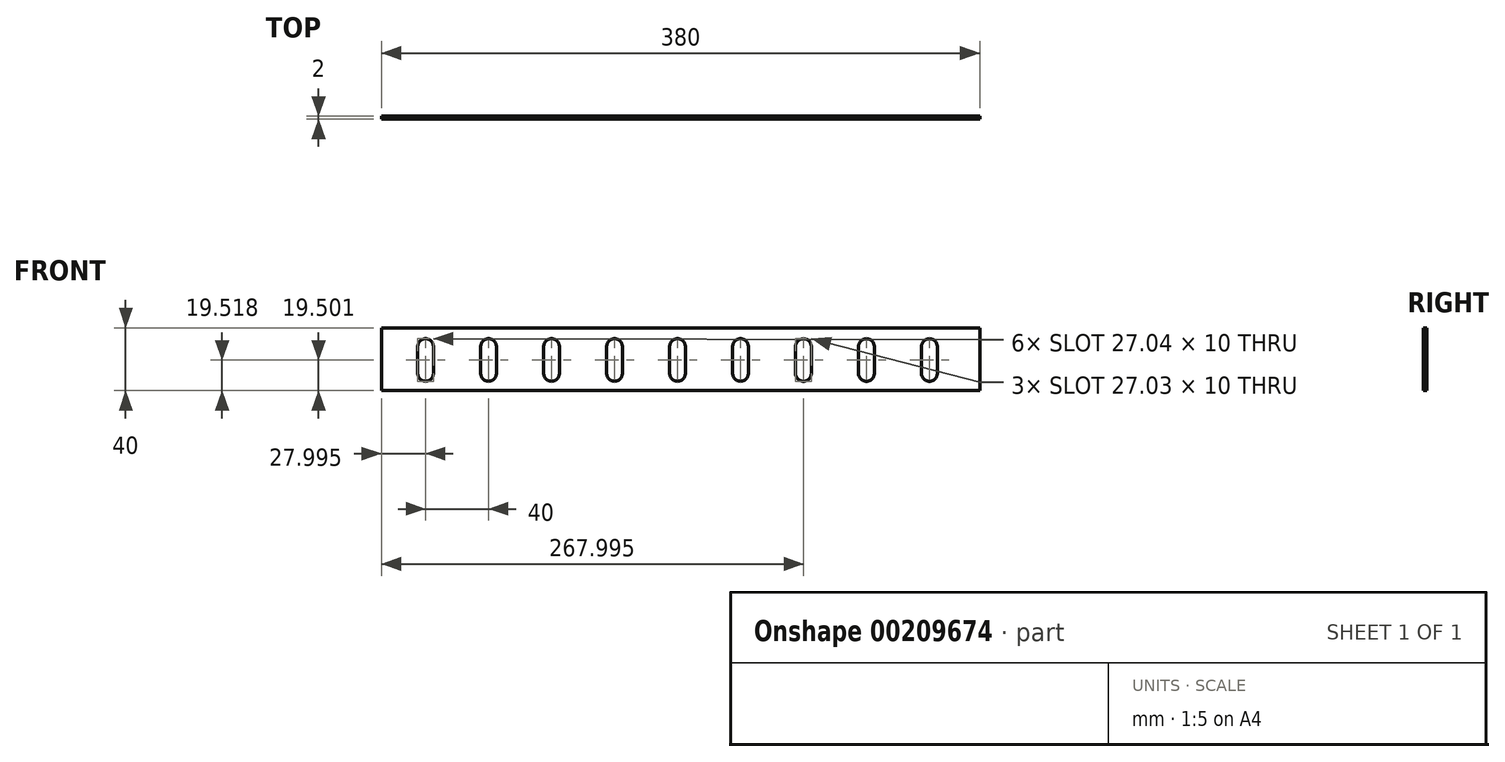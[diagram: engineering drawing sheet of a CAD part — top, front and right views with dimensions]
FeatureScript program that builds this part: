
annotation { "Feature Type Name" : "Feature", "Feature Type Description" : "" }
export const myFeature = defineFeature(function(context is Context, id is Id, definition is map)
    precondition{}
    {
        {
            var Q0;
            Q0=qCreatedBy(makeId("Front.planeOp"),FACE);
            var sketch = newSketch(context, id + "F0", { "sketchPlane" : qUnion([Q0])});
            skLineSegment(sketch, "E0.bottom", {"start": v(171.65, -9.27) * mm, "end": v(-208.35, -9.27) * mm});
            skLineSegment(sketch, "E0.top", {"start": v(171.65, 30.73) * mm, "end": v(-208.35, 30.73) * mm});
            skLineSegment(sketch, "E0.left", {"start": v(171.65, -9.27) * mm, "end": v(171.65, 30.73) * mm});
            skLineSegment(sketch, "E0.right", {"start": v(-208.35, -9.27) * mm, "end": v(-208.35, 30.73) * mm});
            skPoint(sketch, "E0.middle", {"position": v(-20.35, 11.27) * mm});
            skPoint(sketch, "E1", {"position": v(-179.24, -10.73) * mm});
            skLineSegment(sketch, "E2.bottom", {"start": v(-179.24, 21.77) * mm, "end": v(-179.24, 21.77) * mm});
            skLineSegment(sketch, "E2.left", {"start": v(-175.35, 18.77) * mm, "end": v(-175.35, 1.73) * mm});
            skLineSegment(sketch, "E2.right", {"start": v(-185.35, 18.77) * mm, "end": v(-185.35, 1.73) * mm});
            skPoint(sketch, "E3.visualSharp", {"position": v(-185.35, 23.77) * mm});
            skArc(sketch, "E3.filletArc", {"start": v(-180.35, 23.77) * mm, "mid": v(-183.9, 22.3) * mm, "end": v(-185.35, 18.77) * mm});
            skPoint(sketch, "E4.visualSharp", {"position": v(-175.35, 23.77) * mm});
            skArc(sketch, "E4.filletArc", {"start": v(-175.35, 18.77) * mm, "mid": v(-176.82, 22.3) * mm, "end": v(-180.35, 23.77) * mm});
            skPoint(sketch, "E5", {"position": v(-139.24, -10.73) * mm});
            skLineSegment(sketch, "E6.bottom", {"start": v(-139.24, 21.77) * mm, "end": v(-139.24, 21.77) * mm});
            skLineSegment(sketch, "E6.left", {"start": v(-135.35, 18.77) * mm, "end": v(-135.35, 1.73) * mm});
            skLineSegment(sketch, "E6.right", {"start": v(-145.35, 18.77) * mm, "end": v(-145.35, 1.73) * mm});
            skPoint(sketch, "E7.visualSharp", {"position": v(-145.35, 23.77) * mm});
            skArc(sketch, "E7.filletArc", {"start": v(-140.35, 23.77) * mm, "mid": v(-143.9, 22.3) * mm, "end": v(-145.35, 18.77) * mm});
            skPoint(sketch, "E8.visualSharp", {"position": v(-135.35, 23.77) * mm});
            skArc(sketch, "E8.filletArc", {"start": v(-135.35, 18.77) * mm, "mid": v(-136.82, 22.3) * mm, "end": v(-140.35, 23.77) * mm});
            skPoint(sketch, "E9", {"position": v(-99.24, -10.73) * mm});
            skLineSegment(sketch, "E10.bottom", {"start": v(-99.24, 21.77) * mm, "end": v(-99.24, 21.77) * mm});
            skLineSegment(sketch, "E10.left", {"start": v(-95.35, 18.77) * mm, "end": v(-95.35, 1.73) * mm});
            skLineSegment(sketch, "E10.right", {"start": v(-105.35, 18.77) * mm, "end": v(-105.35, 1.73) * mm});
            skPoint(sketch, "E11.visualSharp", {"position": v(-105.35, 23.77) * mm});
            skArc(sketch, "E11.filletArc", {"start": v(-100.35, 23.77) * mm, "mid": v(-103.9, 22.3) * mm, "end": v(-105.35, 18.77) * mm});
            skPoint(sketch, "E12.visualSharp", {"position": v(-95.35, 23.77) * mm});
            skArc(sketch, "E12.filletArc", {"start": v(-95.35, 18.77) * mm, "mid": v(-96.82, 22.3) * mm, "end": v(-100.35, 23.77) * mm});
            skPoint(sketch, "E13", {"position": v(-59.24, -10.73) * mm});
            skLineSegment(sketch, "E14.bottom", {"start": v(-59.24, 21.77) * mm, "end": v(-59.24, 21.77) * mm});
            skLineSegment(sketch, "E14.left", {"start": v(-55.35, 18.77) * mm, "end": v(-55.35, 1.73) * mm});
            skLineSegment(sketch, "E14.right", {"start": v(-65.35, 18.77) * mm, "end": v(-65.35, 1.73) * mm});
            skPoint(sketch, "E15.visualSharp", {"position": v(-65.35, 23.77) * mm});
            skArc(sketch, "E15.filletArc", {"start": v(-60.35, 23.77) * mm, "mid": v(-63.9, 22.3) * mm, "end": v(-65.35, 18.77) * mm});
            skPoint(sketch, "E16.visualSharp", {"position": v(-55.35, 23.77) * mm});
            skArc(sketch, "E16.filletArc", {"start": v(-55.35, 18.77) * mm, "mid": v(-56.82, 22.3) * mm, "end": v(-60.35, 23.77) * mm});
            skPoint(sketch, "E17", {"position": v(-19.24, -10.73) * mm});
            skLineSegment(sketch, "E18.bottom", {"start": v(-19.24, 21.77) * mm, "end": v(-19.24, 21.77) * mm});
            skLineSegment(sketch, "E18.left", {"start": v(-15.35, 18.77) * mm, "end": v(-15.35, 1.73) * mm});
            skLineSegment(sketch, "E18.right", {"start": v(-25.35, 18.77) * mm, "end": v(-25.35, 1.73) * mm});
            skPoint(sketch, "E19.visualSharp", {"position": v(-25.35, 23.77) * mm});
            skArc(sketch, "E19.filletArc", {"start": v(-20.35, 23.77) * mm, "mid": v(-23.9, 22.3) * mm, "end": v(-25.35, 18.77) * mm});
            skPoint(sketch, "E20.visualSharp", {"position": v(-15.35, 23.77) * mm});
            skArc(sketch, "E20.filletArc", {"start": v(-15.35, 18.77) * mm, "mid": v(-16.82, 22.3) * mm, "end": v(-20.35, 23.77) * mm});
            skPoint(sketch, "E21", {"position": v(20.76, -10.73) * mm});
            skLineSegment(sketch, "E22.bottom", {"start": v(20.76, 21.77) * mm, "end": v(20.76, 21.77) * mm});
            skLineSegment(sketch, "E22.left", {"start": v(24.65, 18.77) * mm, "end": v(24.65, 1.73) * mm});
            skLineSegment(sketch, "E22.right", {"start": v(14.65, 18.77) * mm, "end": v(14.65, 1.73) * mm});
            skPoint(sketch, "E23.visualSharp", {"position": v(14.65, 23.77) * mm});
            skArc(sketch, "E23.filletArc", {"start": v(19.65, 23.77) * mm, "mid": v(16.1, 22.3) * mm, "end": v(14.65, 18.77) * mm});
            skPoint(sketch, "E24.visualSharp", {"position": v(24.65, 23.77) * mm});
            skArc(sketch, "E24.filletArc", {"start": v(24.65, 18.77) * mm, "mid": v(23.18, 22.3) * mm, "end": v(19.65, 23.77) * mm});
            skLineSegment(sketch, "E25", {"start": v(-179.24, -5.27) * mm, "end": v(-179.24, -5.27) * mm});
            skPoint(sketch, "E26.visualSharp", {"position": v(-185.35, -3.27) * mm});
            skArc(sketch, "E26.filletArc", {"start": v(-185.35, 1.73) * mm, "mid": v(-183.9, -1.8) * mm, "end": v(-180.35, -3.27) * mm});
            skArc(sketch, "E27.filletArc", {"start": v(-180.35, -3.27) * mm, "mid": v(-176.82, -1.8) * mm, "end": v(-175.35, 1.73) * mm});
            skLineSegment(sketch, "E28", {"start": v(-139.24, -5.27) * mm, "end": v(-139.24, -5.27) * mm});
            skLineSegment(sketch, "E29", {"start": v(-99.24, -5.27) * mm, "end": v(-99.24, -5.27) * mm});
            skLineSegment(sketch, "E30", {"start": v(-59.24, -5.27) * mm, "end": v(-59.24, -5.27) * mm});
            skLineSegment(sketch, "E31", {"start": v(-19.24, -5.27) * mm, "end": v(-19.24, -5.27) * mm});
            skLineSegment(sketch, "E32", {"start": v(20.76, -5.27) * mm, "end": v(20.76, -5.27) * mm});
            skPoint(sketch, "E33.visualSharp", {"position": v(-145.35, -3.27) * mm});
            skArc(sketch, "E33.filletArc", {"start": v(-145.35, 1.73) * mm, "mid": v(-143.9, -1.8) * mm, "end": v(-140.35, -3.27) * mm});
            skPoint(sketch, "E34.visualSharp", {"position": v(-135.35, -3.27) * mm});
            skArc(sketch, "E34.filletArc", {"start": v(-140.35, -3.27) * mm, "mid": v(-136.82, -1.8) * mm, "end": v(-135.35, 1.73) * mm});
            skPoint(sketch, "E35.visualSharp", {"position": v(-105.35, -3.27) * mm});
            skArc(sketch, "E35.filletArc", {"start": v(-105.35, 1.73) * mm, "mid": v(-103.9, -1.8) * mm, "end": v(-100.35, -3.27) * mm});
            skPoint(sketch, "E36.visualSharp", {"position": v(-95.35, -3.27) * mm});
            skArc(sketch, "E36.filletArc", {"start": v(-100.35, -3.27) * mm, "mid": v(-96.82, -1.8) * mm, "end": v(-95.35, 1.73) * mm});
            skPoint(sketch, "E37.visualSharp", {"position": v(-65.35, -3.27) * mm});
            skArc(sketch, "E37.filletArc", {"start": v(-65.35, 1.73) * mm, "mid": v(-63.9, -1.8) * mm, "end": v(-60.35, -3.27) * mm});
            skPoint(sketch, "E38.visualSharp", {"position": v(-55.35, -3.27) * mm});
            skArc(sketch, "E38.filletArc", {"start": v(-60.35, -3.27) * mm, "mid": v(-56.82, -1.8) * mm, "end": v(-55.35, 1.73) * mm});
            skPoint(sketch, "E39.visualSharp", {"position": v(-25.35, -3.27) * mm});
            skArc(sketch, "E39.filletArc", {"start": v(-25.35, 1.73) * mm, "mid": v(-23.9, -1.8) * mm, "end": v(-20.35, -3.27) * mm});
            skPoint(sketch, "E40.visualSharp", {"position": v(-15.35, -3.27) * mm});
            skArc(sketch, "E40.filletArc", {"start": v(-20.35, -3.27) * mm, "mid": v(-16.82, -1.8) * mm, "end": v(-15.35, 1.73) * mm});
            skPoint(sketch, "E41.visualSharp", {"position": v(14.65, -3.27) * mm});
            skArc(sketch, "E41.filletArc", {"start": v(14.65, 1.73) * mm, "mid": v(16.1, -1.8) * mm, "end": v(19.65, -3.27) * mm});
            skPoint(sketch, "E42.visualSharp", {"position": v(24.65, -3.27) * mm});
            skArc(sketch, "E42.filletArc", {"start": v(19.65, -3.27) * mm, "mid": v(23.18, -1.8) * mm, "end": v(24.65, 1.73) * mm});
            skPoint(sketch, "E43.middle", {"position": v(94.23, 11.25) * mm});
            skLineSegment(sketch, "E44.bottom", {"start": v(55.34, 21.75) * mm, "end": v(55.34, 21.75) * mm});
            skLineSegment(sketch, "E44.left", {"start": v(64.65, 18.75) * mm, "end": v(64.65, 1.71) * mm});
            skLineSegment(sketch, "E44.right", {"start": v(54.65, 18.75) * mm, "end": v(54.65, 1.71) * mm});
            skPoint(sketch, "E45.visualSharp", {"position": v(54.65, 23.75) * mm});
            skArc(sketch, "E45.filletArc", {"start": v(54.77, 19.87) * mm, "mid": v(54.68, 19.31) * mm, "end": v(54.65, 18.75) * mm});
            skPoint(sketch, "E46.visualSharp", {"position": v(64.65, 23.75) * mm});
            skArc(sketch, "E46.filletArc", {"start": v(64.65, 18.75) * mm, "mid": v(60.2, 23.72) * mm, "end": v(54.77, 19.87) * mm});
            skLineSegment(sketch, "E47.bottom", {"start": v(95.34, 21.75) * mm, "end": v(95.34, 21.75) * mm});
            skLineSegment(sketch, "E47.left", {"start": v(104.65, 18.75) * mm, "end": v(104.65, 1.71) * mm});
            skLineSegment(sketch, "E47.right", {"start": v(94.65, 18.75) * mm, "end": v(94.65, 1.71) * mm});
            skPoint(sketch, "E48.visualSharp", {"position": v(94.65, 23.75) * mm});
            skArc(sketch, "E48.filletArc", {"start": v(94.77, 19.87) * mm, "mid": v(94.68, 19.31) * mm, "end": v(94.65, 18.75) * mm});
            skPoint(sketch, "E49.visualSharp", {"position": v(104.65, 23.75) * mm});
            skArc(sketch, "E49.filletArc", {"start": v(104.65, 18.75) * mm, "mid": v(100.2, 23.72) * mm, "end": v(94.77, 19.87) * mm});
            skLineSegment(sketch, "E50.bottom", {"start": v(135.34, 21.75) * mm, "end": v(135.34, 21.75) * mm});
            skLineSegment(sketch, "E50.left", {"start": v(144.65, 18.75) * mm, "end": v(144.65, 1.71) * mm});
            skLineSegment(sketch, "E50.right", {"start": v(134.65, 18.75) * mm, "end": v(134.65, 1.71) * mm});
            skPoint(sketch, "E51.visualSharp", {"position": v(134.65, 23.75) * mm});
            skArc(sketch, "E51.filletArc", {"start": v(134.77, 19.87) * mm, "mid": v(134.68, 19.31) * mm, "end": v(134.65, 18.75) * mm});
            skPoint(sketch, "E52.visualSharp", {"position": v(144.65, 23.75) * mm});
            skArc(sketch, "E52.filletArc", {"start": v(144.65, 18.75) * mm, "mid": v(140.2, 23.72) * mm, "end": v(134.77, 19.87) * mm});
            skLineSegment(sketch, "E53", {"start": v(55.34, -5.29) * mm, "end": v(55.34, -5.29) * mm});
            skLineSegment(sketch, "E54", {"start": v(95.34, -5.29) * mm, "end": v(95.34, -5.29) * mm});
            skLineSegment(sketch, "E55", {"start": v(135.34, -5.29) * mm, "end": v(135.34, -5.29) * mm});
            skPoint(sketch, "E56.visualSharp", {"position": v(54.65, -3.29) * mm});
            skArc(sketch, "E56.filletArc", {"start": v(54.65, 1.71) * mm, "mid": v(54.65, 1.54) * mm, "end": v(54.66, 1.36) * mm});
            skPoint(sketch, "E57.visualSharp", {"position": v(64.65, -3.29) * mm});
            skArc(sketch, "E57.filletArc", {"start": v(54.66, 1.36) * mm, "mid": v(59.82, -3.28) * mm, "end": v(64.65, 1.71) * mm});
            skPoint(sketch, "E58.visualSharp", {"position": v(94.65, -3.29) * mm});
            skArc(sketch, "E58.filletArc", {"start": v(94.65, 1.71) * mm, "mid": v(94.65, 1.54) * mm, "end": v(94.66, 1.36) * mm});
            skPoint(sketch, "E59.visualSharp", {"position": v(104.65, -3.29) * mm});
            skArc(sketch, "E59.filletArc", {"start": v(94.66, 1.36) * mm, "mid": v(99.82, -3.28) * mm, "end": v(104.65, 1.71) * mm});
            skPoint(sketch, "E60.visualSharp", {"position": v(134.65, -3.29) * mm});
            skArc(sketch, "E60.filletArc", {"start": v(134.65, 1.71) * mm, "mid": v(134.65, 1.54) * mm, "end": v(134.66, 1.36) * mm});
            skPoint(sketch, "E61.visualSharp", {"position": v(144.65, -3.29) * mm});
            skArc(sketch, "E61.filletArc", {"start": v(134.66, 1.36) * mm, "mid": v(139.82, -3.28) * mm, "end": v(144.65, 1.71) * mm});
            skSolve(sketch);
        }
        {
            var Q0;
            Q0=makeQuery(id+"F0.imprint","IMPRINT",FACE,{"disambiguationData":[TD([[makeQuery(id+"F0.imprint","IMPRINT",EDGE,{"derivedFrom":sQuery(id+"F0.wireOp",EDGE,"E0.bottom")}),-1.0]])]});
            extrude(context, id + "F1", {"entities" : qUnion([Q0]), "depth" : 2 * mm});
        }
    });
